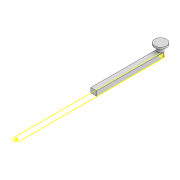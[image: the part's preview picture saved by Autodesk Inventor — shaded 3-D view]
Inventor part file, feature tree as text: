
AUTODESK INVENTOR PART (.ipt)
format: ipt  version: 2022 (Build 260153000, 153)  size: 118,784 bytes
history: native  units: mm
features: sketch x5, extrude x4, projected_geometry x2
ambient origin geometry x8: Origin, YZ Plane, XZ Plane, XY Plane, X Axis, Y Axis, Z Axis, Center Point
bodies: Solid1 (feature_tree)
feature tree (11):
  extrude  "Extrusion1"  Depth=10.0mm
  extrude  "Extrusion2"  Depth=3.0mm
  sketch  "Sketch3"  dims[d4=8.0mm d5=0.0mm d12=10.0mm]
  extrude  "Extrusion3"  Depth=10.0mm
  extrude  "Extrusion4"  Depth=20.0mm
  sketch  "Sketch1"  dims[d0=244.795mm d1=10.0mm]
  sketch  "Sketch2"  dims[d2=3.0mm d3=3.0mm]
  projected_geometry  "Projected Loop1"
  projected_geometry  "Projected Loop2"
  sketch  "Sketch4"  dims[d13=12.0mm d14=0.0mm d15=20.0mm]
  sketch  "Sketch5"  dims[d16=3.0mm d17=0.0mm d18=100.0mm d19=0.0mm]
